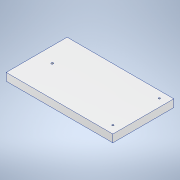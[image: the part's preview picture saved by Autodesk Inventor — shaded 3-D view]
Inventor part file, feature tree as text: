
AUTODESK INVENTOR PART (.ipt)
format: ipt  version: 2022 (Build 260153000, 153)  size: 113,664 bytes
history: native  units: in
note: dims shown in document units (in); Inventor stores cm internally (conversion verified against a paired STEP export)
features: sketch x3, hole x2, extrude x1
ambient origin geometry x8: Origin, YZ Plane, XZ Plane, XY Plane, X Axis, Y Axis, Z Axis, Center Point
bodies: Solid1 (feature_tree)
feature tree (6):
  extrude  "Extrusion1"  Depth=2.0in
  hole  "Hole1"  [1 undecoded]
  hole  "Hole2"  [1 undecoded]
  sketch  "Sketch1"  dims[d0=3.5in d1=2.0in]
  sketch  "Sketch2"  dims[d2=0.25in d3=0.0in d4=0.25in]
  sketch  "Sketch3"  dims[d5=1.525in d6=0.25in d7=0.0561in d8=0.146in d9=0.119in d10=0.25in d11=0.5635in d12=1.0in d13=0.8108in d14=0.5in d15=1.0125in d16=0.0667in d17=0.172in d18=0.375in d19=0.25in d20=0.5635in d21=1.0in d22=0.8108in]
note: 2 required parameter values undecoded (feature->parameter linkage not recoverable at this tier; creation-order binding heuristic only, values carry confidence <= 0.55)
